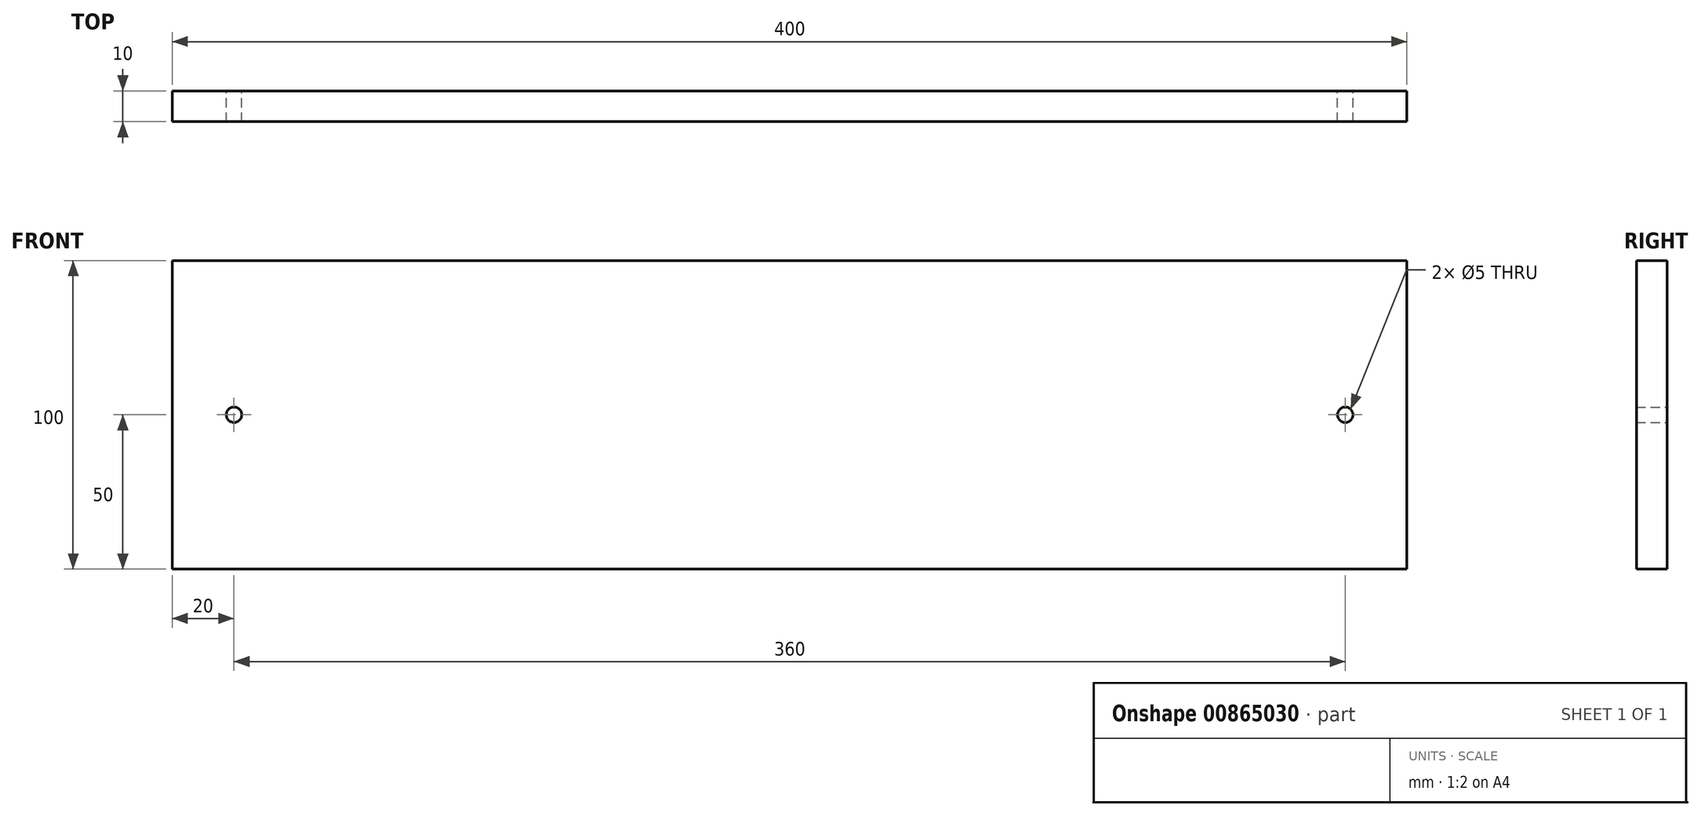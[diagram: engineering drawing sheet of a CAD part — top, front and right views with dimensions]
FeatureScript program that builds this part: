
annotation { "Feature Type Name" : "Feature", "Feature Type Description" : "" }
export const myFeature = defineFeature(function(context is Context, id is Id, definition is map)
    precondition{}
    {
        {
            var Q0;
            Q0=qCreatedBy(makeId("Front.planeOp"),FACE);
            var sketch = newSketch(context, id + "F0", { "sketchPlane" : qUnion([Q0])});
            skLineSegment(sketch, "E0", {"start": v(0, 0) * mm, "end": v(400, 0) * mm});
            skLineSegment(sketch, "E1", {"start": v(400, 0) * mm, "end": v(400, -100) * mm});
            skLineSegment(sketch, "E2", {"start": v(400, -100) * mm, "end": v(0, -100) * mm});
            skLineSegment(sketch, "E3", {"start": v(0, -100) * mm, "end": v(0, 0) * mm});
            skLineSegment(sketch, "E4", {"start": v(40, 0) * mm, "end": v(40, -100) * mm, "construction": true});
            skLineSegment(sketch, "E5", {"start": v(360, 0) * mm, "end": v(360, -100) * mm, "construction": true});
            skLineSegment(sketch, "E6", {"start": v(40, -50) * mm, "end": v(0, -50) * mm, "construction": true});
            skLineSegment(sketch, "E7", {"start": v(360, -50) * mm, "end": v(400, -50) * mm, "construction": true});
            skPoint(sketch, "E8", {"position": v(20, -50) * mm});
            skPoint(sketch, "E9", {"position": v(380, -50) * mm});
            skSolve(sketch);
        }
        {
            var Q0;
            Q0=makeQuery(id+"F0.imprint","IMPRINT",FACE,{"disambiguationData":[TD([[makeQuery(id+"F0.imprint","IMPRINT",EDGE,{"derivedFrom":sQuery(id+"F0.wireOp",EDGE,"E0")}),-1.0]])]});
            extrude(context, id + "F1", {"entities" : qUnion([Q0]), "depth" : 10 * mm, "offsetDistance" : 25 * mm});
        }
        {
            var Q0;
            Q0=sQuery(id+"F0.wireOp",VERTEX,"E9");
            var Q1;
            Q1=sQuery(id+"F0.wireOp",VERTEX,"E8");
            var Q2;
            Q2=makeQuery(id+"F1.opExtrude","SWEPT_BODY",BODY,{"disambiguationData":[OSD([sQuery(id+"F0.wireOp",EDGE,"E0"),sQuery(id+"F0.wireOp",EDGE,"E1"),sQuery(id+"F0.wireOp",EDGE,"E2"),sQuery(id+"F0.wireOp",EDGE,"E3")])]});
            hole(context, id + "F2", {"style" : HoleStyle.SIMPLE, "endStyle" : HoleEndStyle.THROUGH, "oppositeDirection" : true, "holeDiameter" : 5 * mm, "majorDiameter" : 5 * mm, "isTappedThrough" : true, "tappedDepth" : 12 * mm, "tapClearance" : 3, "locations" : qUnion([Q0, Q1]), "scope" : qUnion([Q2])});
        }
    });
